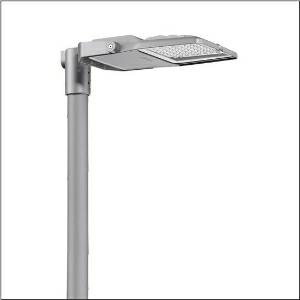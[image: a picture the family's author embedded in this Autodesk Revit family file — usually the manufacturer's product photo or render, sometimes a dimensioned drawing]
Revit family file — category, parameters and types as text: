
# Revit family: floodlight_fl_21_iq_mini___pl43_5xa7771c4a3a_be4f
name_source: partatom
category: Lighting Fixtures
units: mm (PartAtom-declared; Revit-internal decimal feet)

## family parameters
Cut with Voids When Loaded = No
Host = Face
Light Source = No
Part Type = Normal
Room Calculation Point = No
Round Connector Dimension = Use Diameter
Shared = No

## types (1)
- --- (1 x LED, 13050 lm, 87.2 W, 4000K)
    Apparent Load = 87 VA
    CIE Flux Codes = 27 78 99 100 100
    Color Rendering = 70
    Color Temperature = 4000K
    Default Elevation = 1800 mm
    Description = Floodlight FL 21 iQ mini, floodlight, primary light control with lens, of PMMA, primary optical cover: protective disc, of toughened safety glass, transparent, light distribution: PL43, light emission: direct distribution, installation type: surface-mounted, LED, High Power LED, rated luminous flux: 13.050lm, luminous efficacy: 150lm/W, light colour: 740, colour temperature: 4000K, control gear: iQ Comfort/DALI, control: Auto-Match, Temp-Guard, Lumen-Switch, Night-Set, Smart-Wire, Light-Fading, Desk-Remote (wireless, voltage-free reading and setting of iQ features in the workshop via application-optimized NFC function/RFID function), optimised constant luminous flux control (CLO 2.0), with terminal, 6-pole, mains connection: 220..240V, AC, 50/60Hz, start of lifetime: 87W, end of service life: 92W, reduction: 40W, luminaire housing, of diecast aluminium, powder-coated, Siteco® metallic grey (DB 702S), corrosivity category C5 mid according to DIN EN ISO 12944, suitable for swimming pools, chlorine-resistant, sealing non-destructively replaceable, please order mast flange separately, mast bracket, of steel, galvanised, powder-coated, Siteco® metallic grey (DB 702S), protection rating (complete): IP66, insulation class (complete): insulation class II (safety insulation), certification: CE, ENEC, VDE, protection symbol: D, impact resistance: IK08, permissible operating ambient temperature: -40..+40°C, permissible operating ambient temperature for outdoor applications: -40..+50°C, standard: DIN EN 12944, LABS conformity tested according to VDMA 24364:2018-05, packaging unit: 1 piece

Light Distribution: PL43
    Height = 70 mm
    Lamp = 1 x LED
    Lamp Light Flux = 13050 lm
    Lamp Power = 87.2 W
    Lamp count = 1
    Length = 485 mm
    Luminous efficacy = 150 lm/W
    Manufacturer = Siteco
    ModVariant = No
    Model = 5XA7771C4A3A
    Number of Poles = 1
    OnlyDefault = Yes
    Power Factor = 1
    Product Name = Floodlight FL 21 iQ mini | PL43
    Product group = floodlight | pylon annexe
    ProductGroupID = 6201
    Protection Class = Protection class II
    Protection Degree = IP 66
    RLX_Detail_Level = 1
    RLX_Emergency_Light_Flux = 0 lm
    RLX_Emergency_Type = 0
    RLX_Emergency_Type_DB = No
    RlxData = <blob elided: 101261 chars, md5=3e020aee>
    Socket = socket
    Standby Power = 0 W
    System Light Flux = 13050 lm
    System Power = 87 W
    Type Comments = factory setting: luminous flux: 100 % | dim-lin: 254 | 456 mA
    Type Image = l_1007125.jpg
    URL = http://relux.com
    VarID = @adj_183879
    Voltage = 0 V
    Weight = 0.00 kg
    Width = 337 mm

## geometry (parser evidence)
native form markers: Blend x4, Sweep x10
no freeform markers — native parametric forms only
